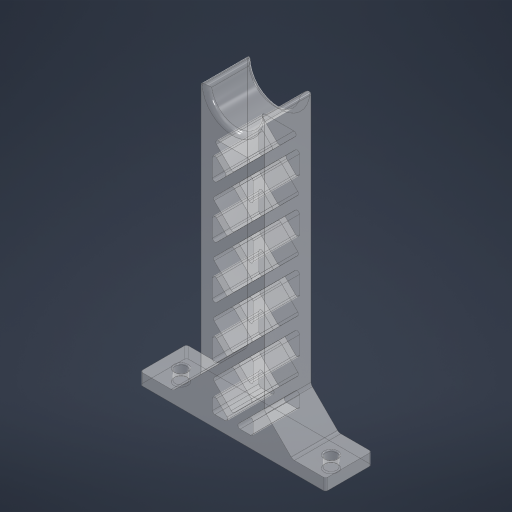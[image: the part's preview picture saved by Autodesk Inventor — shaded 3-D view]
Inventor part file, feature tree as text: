
AUTODESK INVENTOR PART (.ipt)
format: ipt  version: 2024.2 (Build 282272000, 272)  size: 499,200 bytes
history: native  units: mm
features: fillet x5, extrude x3, sketch x3, projected_geometry x2, chamfer x1
ambient origin geometry x8: Origin, YZ Plane, XZ Plane, XY Plane, X Axis, Y Axis, Z Axis, Center Point
bodies: Solid1 (feature_tree)
feature tree (14):
  extrude  "Extrusion1"  Depth=11.25mm
  fillet  "Fillet1"  Radius=11.25mm
  fillet  "Fillet2"  Radius=27.5mm
  chamfer  "Chamfer1"  Distance=5.0mm
  extrude  "Extrusion2"  Depth=20.0mm TaperAngle=0.0deg
  fillet  "Fillet3"  Radius=2.0mm
  fillet  "Fillet4"  Radius=1.0mm
  extrude  "Extrusion3"  Depth=2.0mm TaperAngle=45.0deg
  fillet  "Fillet5"  Radius=5.0mm
  sketch  "Sketch1"  dims[d0=115.0mm d1=22.5mm d2=11.25mm d3=27.5mm]
  sketch  "Sketch2"  dims[d4=40.0mm]
  projected_geometry  "Projected Loop1"
  projected_geometry  "Projected Loop2"
  sketch  "Sketch3"  dims[d5=40.0mm d6=5.0mm d7=20.0mm d8=0.0mm d9=2.0mm d10=1.0mm d11=12.0mm d12=2.0mm d13=45.0deg d14=5.0mm d15=5.0mm d16=10.0mm d17=7.625mm d18=14.25mm d19=7.625mm d20=7.625mm d21=10.0mm d22=20.0mm d23=0.0mm d24=0.5mm d25=2.0mm d26=0.0mm d27=5.0mm d28=5.0mm d29=5.0mm d30=45.0deg d31=5.0mm d32=5.0mm d33=45.0deg d34=5.0mm d35=5.0mm d36=5.0mm d37=5.0mm d38=45.0deg d39=5.0mm d40=5.0mm d41=20.0mm d42=0.0mm d43=1.0mm]
